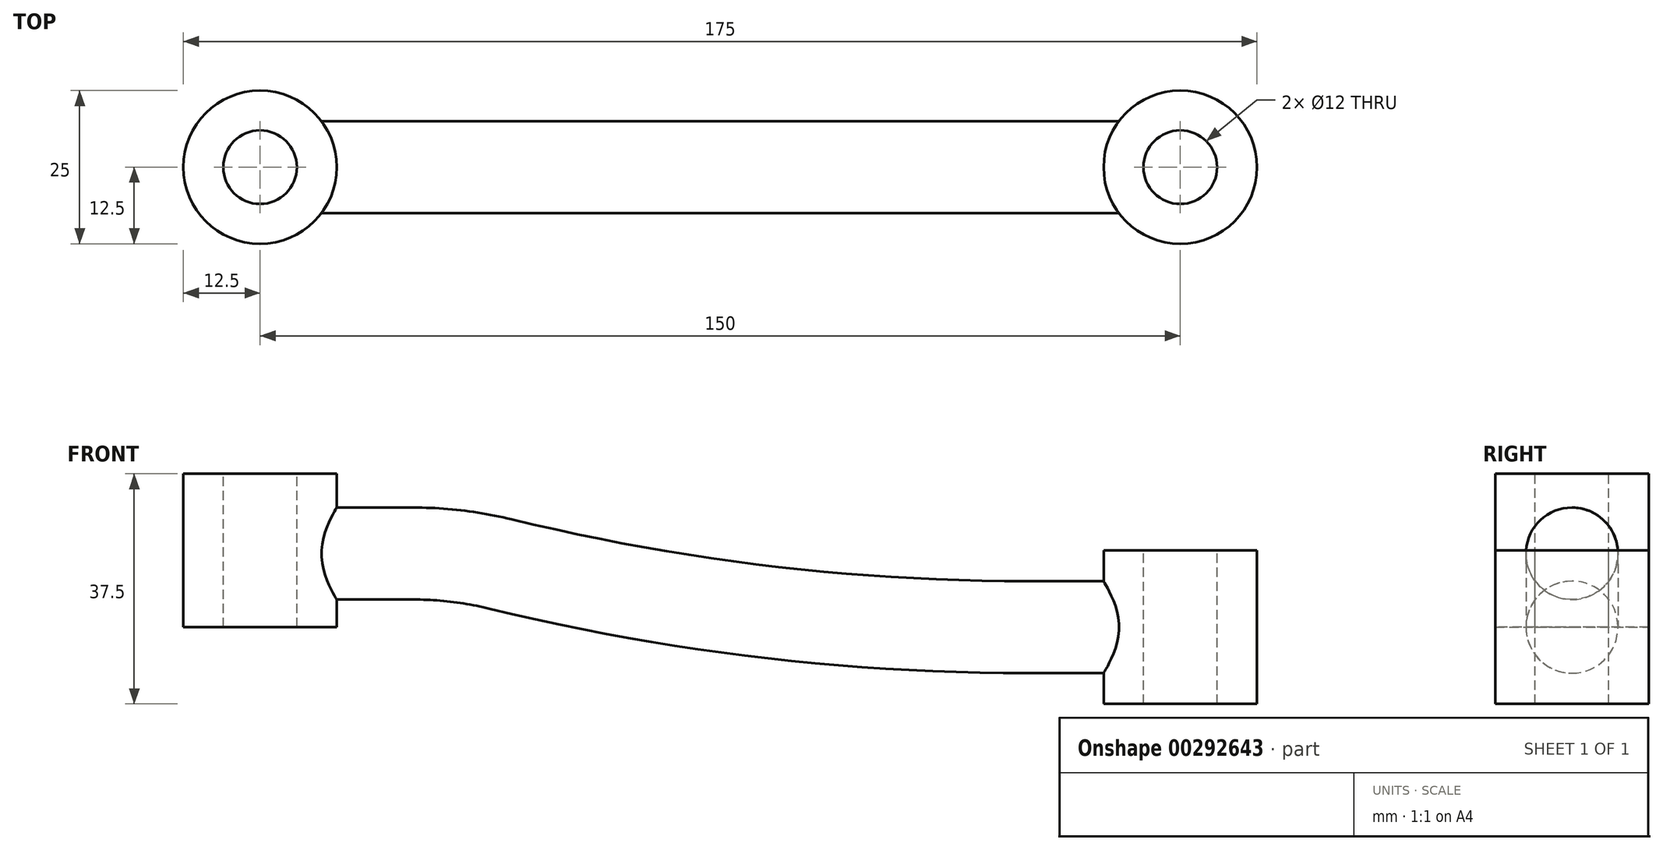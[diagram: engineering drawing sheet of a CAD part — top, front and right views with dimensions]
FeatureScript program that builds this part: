
annotation { "Feature Type Name" : "Feature", "Feature Type Description" : "" }
export const myFeature = defineFeature(function(context is Context, id is Id, definition is map)
    precondition{}
    {
        {
            var Q0;
            Q0=qCreatedBy(makeId("Top.planeOp"),FACE);
            var sketch = newSketch(context, id + "F0", { "sketchPlane" : qUnion([Q0])});
            skCircle(sketch, "E0", {"center": v(0, 0) * mm, "radius": 12.5 * mm});
            skCircle(sketch, "E1", {"center": v(150, 0) * mm, "radius": 12.5 * mm});
            skSolve(sketch);
        }
        {
            var Q0;
            Q0=makeQuery(id+"F0.imprint","IMPRINT",FACE,{"disambiguationData":[TD([[makeQuery(id+"F0.imprint","IMPRINT",EDGE,{"derivedFrom":sQuery(id+"F0.wireOp",EDGE,"E0")}),1.0]])]});
            extrude(context, id + "F1", {"entities" : qUnion([Q0]), "depth" : 25 * mm});
        }
        {
            var Q0;
            Q0=makeQuery(id+"F0.imprint","IMPRINT",FACE,{"disambiguationData":[TD([[makeQuery(id+"F0.imprint","IMPRINT",EDGE,{"derivedFrom":sQuery(id+"F0.wireOp",EDGE,"E1")}),1.0]])]});
            extrude(context, id + "F2", {"entities" : qUnion([Q0]), "depth" : 25 * mm, "symmetric" : true});
        }
        {
            var Q0;
            Q0=qCreatedBy(makeId("Front.planeOp"),FACE);
            var sketch = newSketch(context, id + "F3", { "sketchPlane" : qUnion([Q0])});
            skLineSegment(sketch, "E2", {"start": v(0, 12) * mm, "end": v(25, 12) * mm});
            skArc(sketch, "E3", {"start": v(25, 12) * mm, "mid": v(32.15, 11.57) * mm, "end": v(39.2, 10.3) * mm});
            skArc(sketch, "E4", {"start": v(39.2, 10.3) * mm, "mid": v(81.79, 2.58) * mm, "end": v(125, 0) * mm});
            skLineSegment(sketch, "E5", {"start": v(125, 0) * mm, "end": v(150, 0) * mm});
            skSolve(sketch);
        }
        {
            var Q0;
            Q0=qCreatedBy(makeId("Right.planeOp"),FACE);
            var sketch = newSketch(context, id + "F4", { "sketchPlane" : qUnion([Q0])});
            skCircle(sketch, "E6", {"center": v(0, 12) * mm, "radius": 7.5 * mm});
            skSolve(sketch);
        }
        {
            var Q0;
            Q0 = qSketchRegion(id + "F4", true);
            var Q1;
            Q1 = qConstructionFilter(qBodyType(qCreatedBy(id + "F3" ,EDGE), BodyType.WIRE), ConstructionObject.NO);
            sweep(context, id + "F5", {"operationType" : NewBodyOperationType.ADD, "profiles" : qUnion([Q0]), "path" : qUnion([Q1])});
        }
        {
            var Q0;
            Q0=makeQuery(id+"F1.opExtrude","CAP_FACE",FACE,{"disambiguationData":[OSD([sQuery(id+"F0.wireOp",EDGE,"E0")])],"isStart":false});
            var sketch = newSketch(context, id + "F6", { "sketchPlane" : qUnion([Q0])});
            skCircle(sketch, "E7", {"center": v(0, 0) * mm, "radius": 6 * mm});
            skCircle(sketch, "E8", {"center": v(150, 0) * mm, "radius": 6 * mm});
            skSolve(sketch);
        }
        {
            var Q0;
            Q0 = qSketchRegion(id + "F6", true);
            extrude(context, id + "F7", {"entities" : qUnion([Q0]), "operationType" : NewBodyOperationType.REMOVE, "endBound" : BoundingType.THROUGH_ALL, "oppositeDirection" : true, "depth" : 25 * mm});
        }
    });
